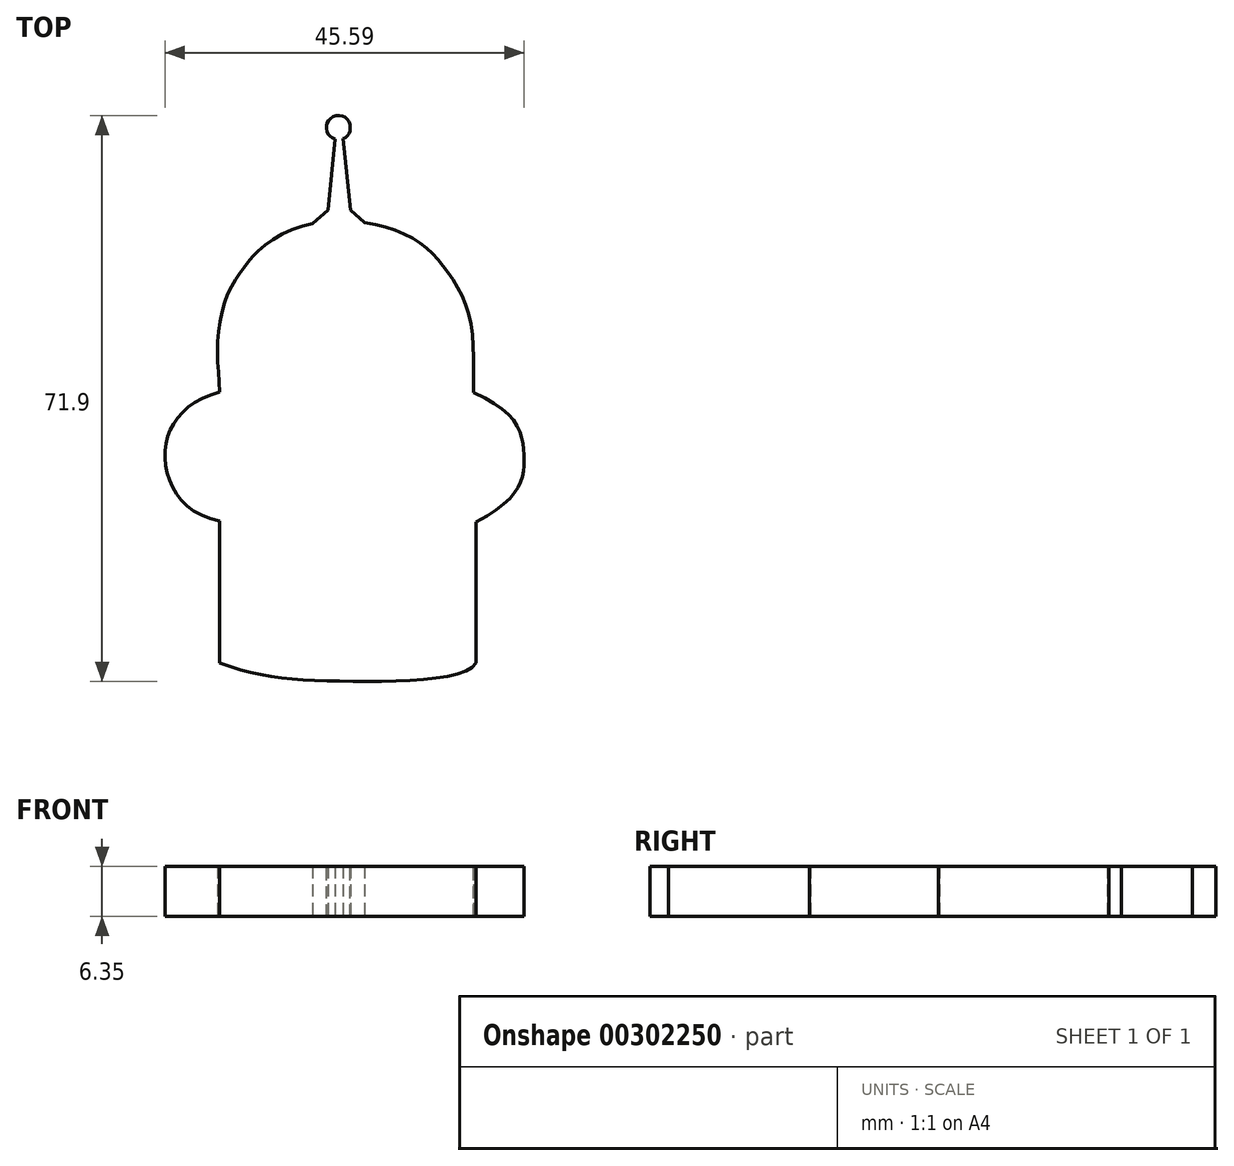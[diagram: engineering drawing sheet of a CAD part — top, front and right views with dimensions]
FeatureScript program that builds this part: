
annotation { "Feature Type Name" : "Feature", "Feature Type Description" : "" }
export const myFeature = defineFeature(function(context is Context, id is Id, definition is map)
    precondition{}
    {
        {
            var Q0;
            Q0=qCreatedBy(makeId("Top.planeOp"),FACE);
            var sketch = newSketch(context, id + "F0", { "sketchPlane" : qUnion([Q0])});
            skLineSegment(sketch, "E0", {"start": v(-17.8, -17.8) * mm, "end": v(-17.8, -30.05) * mm});
            skLineSegment(sketch, "E1", {"start": v(-17.8, -30.05) * mm, "end": v(-17.8, -35.82) * mm});
            skLineSegment(sketch, "E2", {"start": v(14.75, -35.82) * mm, "end": v(14.75, -17.93) * mm});
            skFitSpline(sketch, "E3", {"points": [v(-17.8, -35.82) * mm, v(-2.05, -38.14) * mm, v(14.75, -35.82) * mm], "startDerivative": vector(30.9, -11.43) * mm, "endDerivative": vector(7.95, 13.69) * mm});
            skFitSpline(sketch, "E4", {"points": [v(14.43, -1.5) * mm, v(20.83, -9.79) * mm, v(14.75, -17.93) * mm], "startDerivative": vector(35.65, -15) * mm, "endDerivative": vector(-34.9, -18.74) * mm});
            skFitSpline(sketch, "E5", {"points": [v(-17.8, -17.8) * mm, v(-24.75, -9.16) * mm, v(-17.8, -1.39) * mm], "startDerivative": vector(-29.85, 5.78) * mm, "endDerivative": vector(28.22, 7.68) * mm});
            skFitSpline(sketch, "E6", {"points": [v(0.59, 20.13) * mm, v(7.51, 17.6) * mm, v(11.05, 14) * mm, v(13.89, 8.25) * mm, v(14.43, -1.5) * mm], "startDerivative": vector(32.01, -4.8) * mm, "endDerivative": vector(-0.23, -33.74) * mm});
            skFitSpline(sketch, "E7", {"points": [v(-6.02, 19.97) * mm, v(-12.32, 17.06) * mm, v(-14.75, 14.38) * mm, v(-16.8, 11) * mm, v(-18.06, 5.1) * mm, v(-17.8, -1.39) * mm], "startDerivative": vector(-28.78, -3.45) * mm, "endDerivative": vector(2, -29.2) * mm});
            skLineSegment(sketch, "E8", {"start": v(-2.16, 30.77) * mm, "end": v(-1.2, 21.7) * mm});
            skLineSegment(sketch, "E9", {"start": v(-1.2, 21.7) * mm, "end": v(0.59, 20.13) * mm});
            skLineSegment(sketch, "E10", {"start": v(-6.02, 19.97) * mm, "end": v(-4.03, 21.7) * mm});
            skLineSegment(sketch, "E11", {"start": v(-4.03, 21.7) * mm, "end": v(-3.16, 30.72) * mm});
            skFitSpline(sketch, "E12", {"points": [v(-3.16, 30.72) * mm, v(-4.1, 31.46) * mm, v(-4.2, 32.58) * mm, v(-3.53, 33.52) * mm, v(-2.15, 33.63) * mm, v(-1.33, 32.72) * mm, v(-1.4, 31.43) * mm, v(-2.16, 30.77) * mm], "startDerivative": vector(-8.55, 3.28) * mm, "endDerivative": vector(-7.6, -3.77) * mm});
            skSolve(sketch);
        }
        {
            var Q0;
            Q0 = qSketchRegion(id + "F0", true);
            extrude(context, id + "F1", {"entities" : qUnion([Q0]), "depth" : 6.35 * mm});
        }
    });
